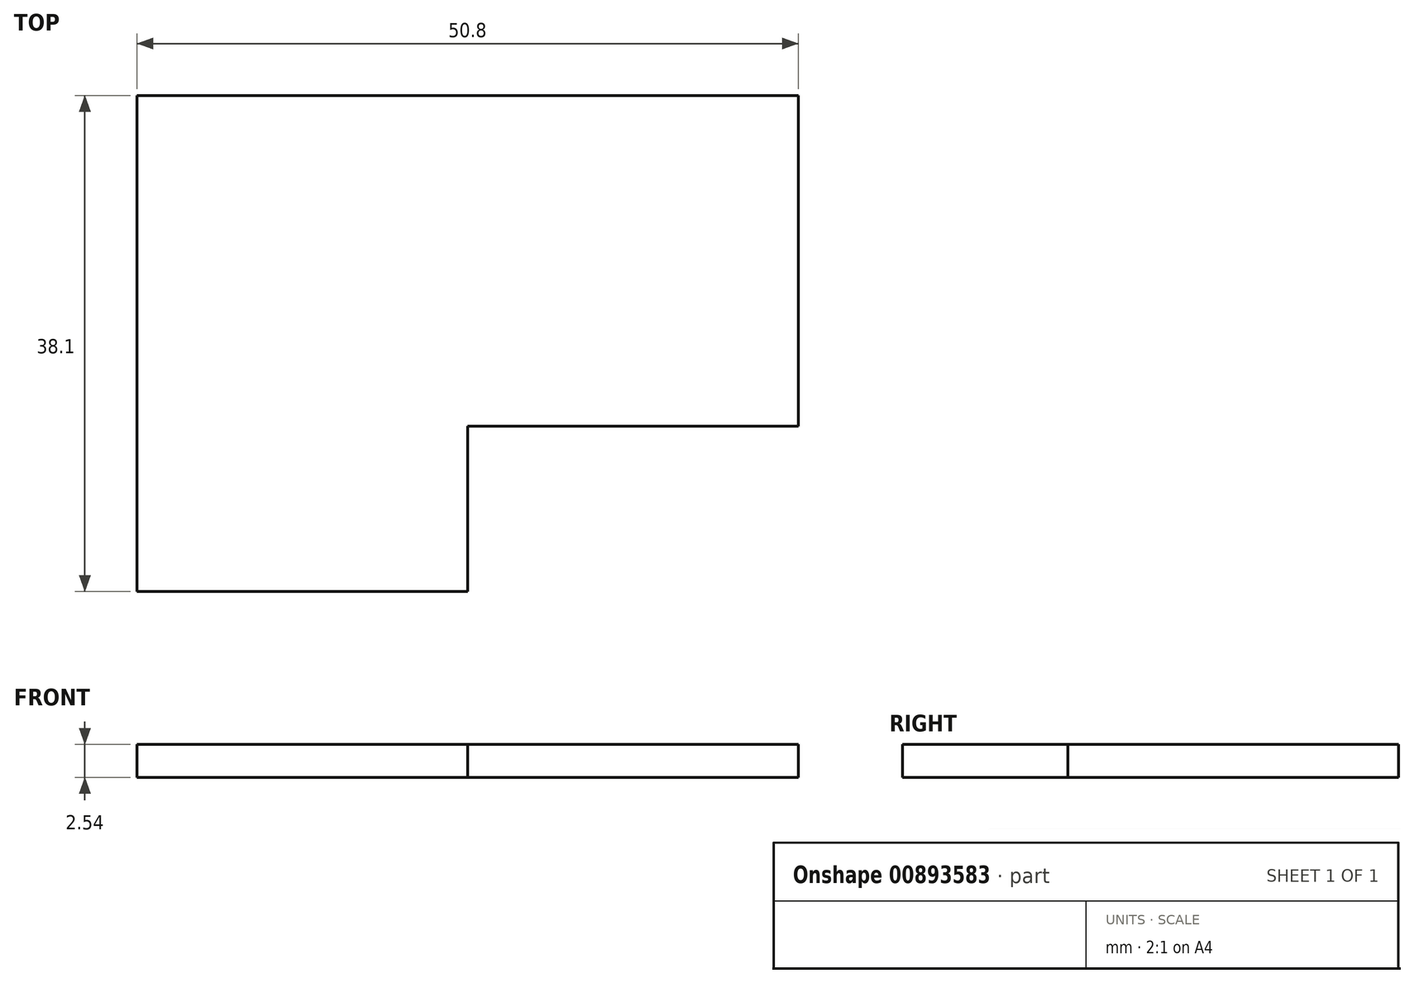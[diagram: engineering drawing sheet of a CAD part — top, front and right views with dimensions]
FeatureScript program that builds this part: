
annotation { "Feature Type Name" : "Feature", "Feature Type Description" : "" }
export const myFeature = defineFeature(function(context is Context, id is Id, definition is map)
    precondition{}
    {
        {
            var Q0;
            Q0=qCreatedBy(makeId("Top.planeOp"),FACE);
            var sketch = newSketch(context, id + "F0", { "sketchPlane" : qUnion([Q0])});
            skLineSegment(sketch, "E0.bottom", {"start": v(-27.86, -3.53) * mm, "end": v(22.94, -3.53) * mm});
            skLineSegment(sketch, "E0.top", {"start": v(-27.86, -41.63) * mm, "end": v(-2.46, -41.63) * mm});
            skLineSegment(sketch, "E0.left", {"start": v(-27.86, -3.53) * mm, "end": v(-27.86, -41.63) * mm});
            skLineSegment(sketch, "E0.right", {"start": v(22.94, -3.53) * mm, "end": v(22.94, -28.93) * mm});
            skLineSegment(sketch, "E1.top", {"start": v(22.94, -28.93) * mm, "end": v(-2.46, -28.93) * mm});
            skLineSegment(sketch, "E1.right", {"start": v(-2.46, -41.63) * mm, "end": v(-2.46, -28.93) * mm});
            skSolve(sketch);
        }
        {
            var Q0;
            Q0 = qSketchRegion(id + "F0", true);
            extrude(context, id + "F1", {"entities" : qUnion([Q0]), "depth" : 2.54 * mm, "offsetDistance" : 25.4 * mm});
        }
    });
